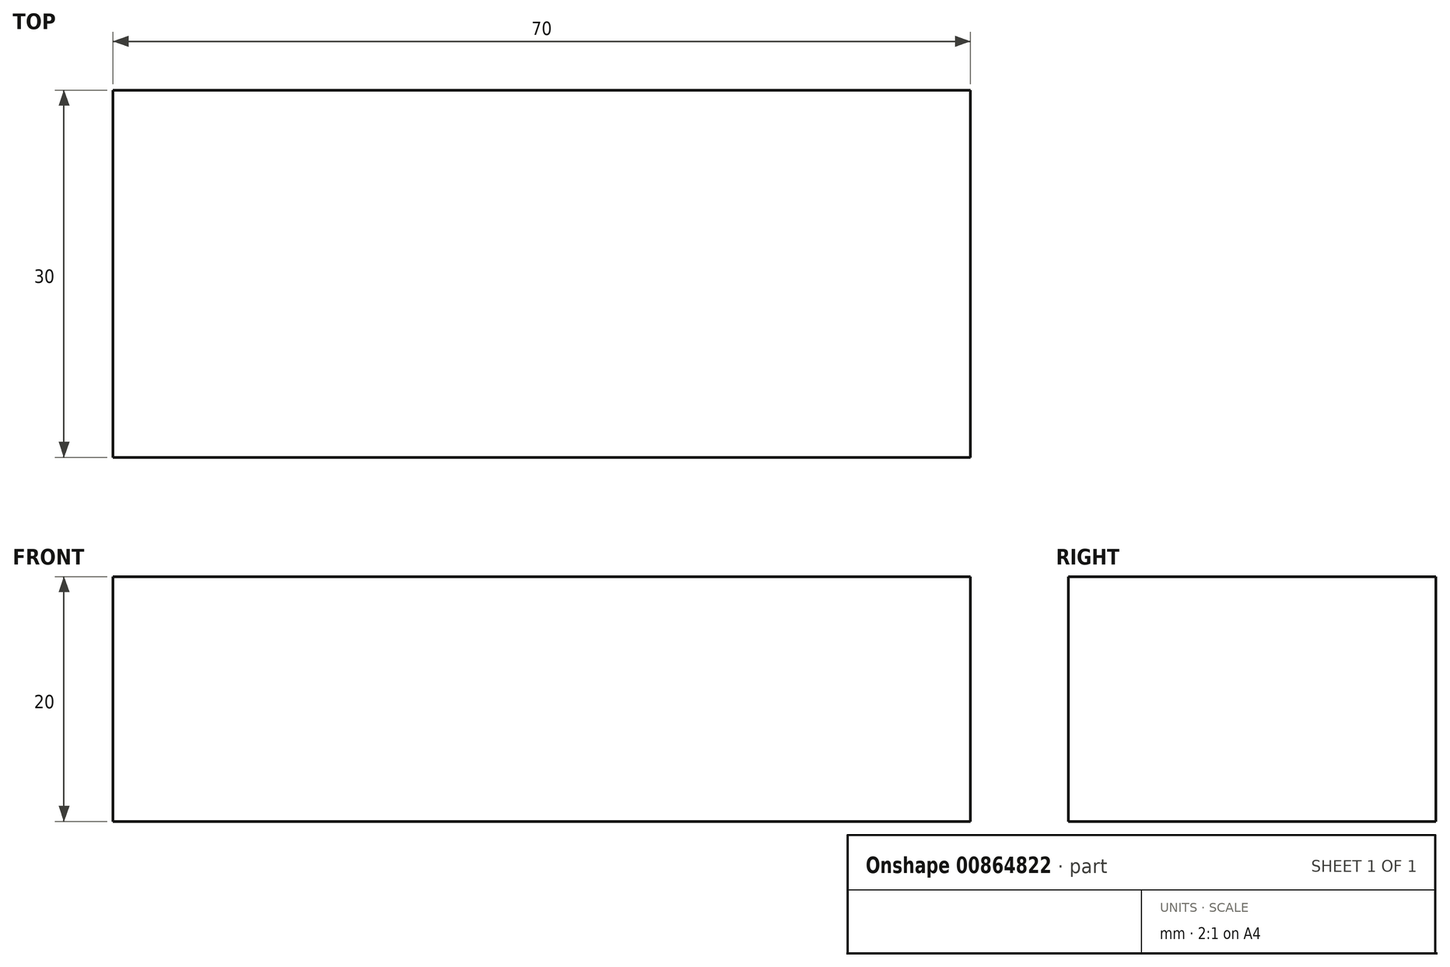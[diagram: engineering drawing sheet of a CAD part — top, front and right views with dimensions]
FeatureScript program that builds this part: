
annotation { "Feature Type Name" : "Feature", "Feature Type Description" : "" }
export const myFeature = defineFeature(function(context is Context, id is Id, definition is map)
    precondition{}
    {
        {
            var Q0;
            Q0=qCreatedBy(makeId("Top.planeOp"),FACE);
            var sketch = newSketch(context, id + "F0", { "sketchPlane" : qUnion([Q0])});
            skLineSegment(sketch, "E0.bottom", {"start": v(-35, 15) * mm, "end": v(35, 15) * mm});
            skLineSegment(sketch, "E0.top", {"start": v(-35, -15) * mm, "end": v(35, -15) * mm});
            skLineSegment(sketch, "E0.left", {"start": v(-35, 15) * mm, "end": v(-35, -15) * mm});
            skLineSegment(sketch, "E0.right", {"start": v(35, 15) * mm, "end": v(35, -15) * mm});
            skPoint(sketch, "E0.middle", {"position": v(0, 0) * mm});
            skSolve(sketch);
        }
        {
            var Q0;
            Q0=makeQuery(id+"F0.imprint","IMPRINT",FACE,{"disambiguationData":[TD([[makeQuery(id+"F0.imprint","IMPRINT",EDGE,{"derivedFrom":sQuery(id+"F0.wireOp",EDGE,"E0.bottom")}),-1.0]])]});
            extrude(context, id + "F1", {"entities" : qUnion([Q0]), "depth" : 20 * mm, "offsetDistance" : 25 * mm});
        }
    });
